# Revit family: PFRD-TMSR-IES TBC
name_source: partatom
category: Lighting Fixtures
units: mm (PartAtom-declared; Revit-internal decimal feet)

## family parameters
Cut with Voids When Loaded = Yes
Host = Face
Light Source = Yes
Maintain Annotation Orientation = No
Part Type = Normal
Room Calculation Point = No
Round Connector Dimension = Use Diameter
Shared = No

## types (2) — shared parameters
CRI = 90
Color Filter = 16777215
Default Elevation = 0' - 0"
Dimming Lamp Color Temperature Shift = <None>
Input Voltage = 120-277V
Lamp = LED
Load Classification = Lighting
Manufacturer = Above All Lighting
Power Factor = 0.9
Tilt Angle = 90.00°
URL = https://www.abovealllighting.com

## per-type parameters (varying)
| type | Lens | Model | Photometric Web File | R | Wattage Comments |
| PFRD20-25W-3000K-TMSR | 0' - 9 3/16" | PFRD20-25-30901-TMSR-WH | PFRD20-25W-3000K.IES | 0' - 9 7/16" | 25W |
| PFRD36-90W-3000K-TMSR | 1' - 5 7/16" | PFRD36-90-30901-TMSR-WH | PFRD36-90W-3000K.IES | 1' - 5 11/16" | 90W |

## geometry (parser evidence)
native form markers: Sweep x1
no freeform markers — native parametric forms only
